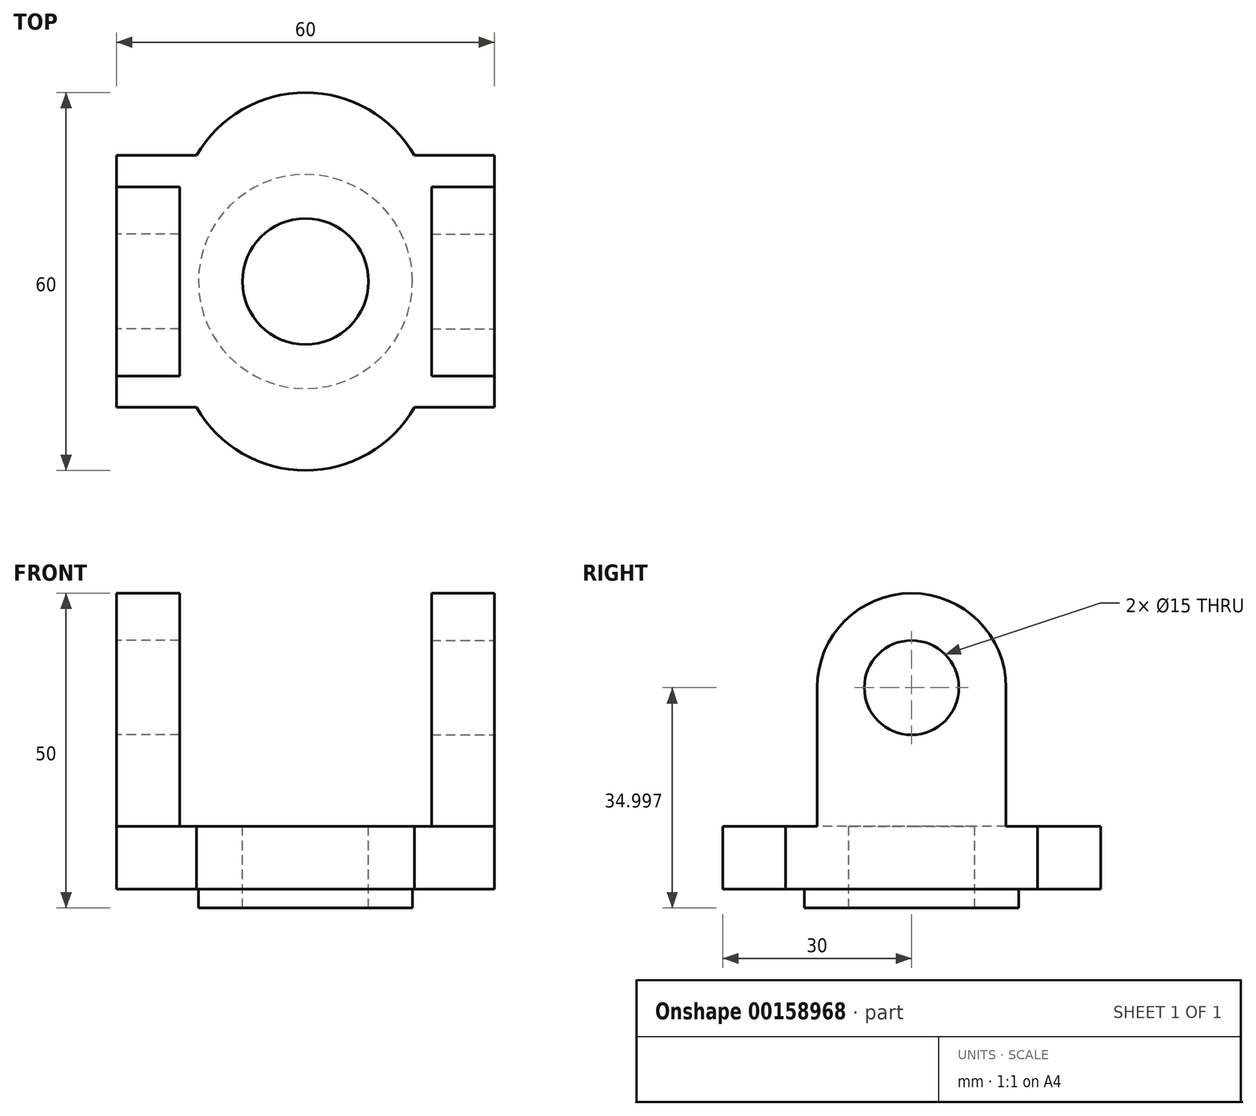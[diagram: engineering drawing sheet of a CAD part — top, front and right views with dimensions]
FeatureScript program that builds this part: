
annotation { "Feature Type Name" : "Feature", "Feature Type Description" : "" }
export const myFeature = defineFeature(function(context is Context, id is Id, definition is map)
    precondition{}
    {
        {
            var Q0;
            Q0=qCreatedBy(makeId("Front.planeOp"),FACE);
            var sketch = newSketch(context, id + "F0", { "sketchPlane" : qUnion([Q0])});
            skLineSegment(sketch, "E0.bottom", {"start": v(-30, -5.63) * mm, "end": v(30, -5.63) * mm});
            skLineSegment(sketch, "E0.top", {"start": v(-30, 4.37) * mm, "end": v(30, 4.37) * mm});
            skLineSegment(sketch, "E0.left", {"start": v(-30, -5.63) * mm, "end": v(-30, 4.37) * mm});
            skLineSegment(sketch, "E0.right", {"start": v(30, -5.63) * mm, "end": v(30, 4.37) * mm});
            skPoint(sketch, "E1", {"position": v(0, 4.37) * mm});
            skPoint(sketch, "E1.positionSnap0", {"position": v(0, 4.37) * mm});
            skSolve(sketch);
        }
        {
            var Q0;
            Q0 = qSketchRegion(id + "F0", true);
            extrude(context, id + "F1", {"entities" : qUnion([Q0]), "oppositeDirection" : true, "depth" : 40 * mm});
        }
        {
            var Q0;
            Q0=makeQuery(id+"F1.opExtrude","SWEPT_FACE",FACE,{"disambiguationData":[OSD([sQuery(id+"F0.wireOp",EDGE,"E0.right")])]});
            var sketch = newSketch(context, id + "F2", { "sketchPlane" : qUnion([Q0])});
            skPoint(sketch, "E2", {"position": v(20, 4.37) * mm});
            skCircle(sketch, "E3", {"center": v(20, 26.37) * mm, "radius": 7.5 * mm});
            skLineSegment(sketch, "E4", {"start": v(5, 4.37) * mm, "end": v(5, 26.37) * mm});
            skPoint(sketch, "E5", {"position": v(35, 4.37) * mm});
            skLineSegment(sketch, "E6", {"start": v(35, 4.37) * mm, "end": v(35, 26.37) * mm});
            skArc(sketch, "E7", {"start": v(35, 26.37) * mm, "mid": v(20, 41.37) * mm, "end": v(5, 26.37) * mm});
            skLineSegment(sketch, "E8", {"start": v(5, 4.37) * mm, "end": v(35, 4.37) * mm});
            skSolve(sketch);
        }
        {
            var Q0;
            Q0 = qSketchRegion(id + "F2", true);
            extrude(context, id + "F3", {"entities" : qUnion([Q0]), "operationType" : NewBodyOperationType.ADD, "oppositeDirection" : true, "depth" : 10 * mm});
        }
        {
            var Q0;
            Q0=makeQuery(id+"F1.opExtrude","SWEPT_FACE",FACE,{"disambiguationData":[OSD([sQuery(id+"F0.wireOp",EDGE,"E0.left")])]});
            var sketch = newSketch(context, id + "F4", { "sketchPlane" : qUnion([Q0])});
            skPoint(sketch, "E9", {"position": v(-35, 4.37) * mm});
            skPoint(sketch, "E10", {"position": v(-5, 4.37) * mm});
            skLineSegment(sketch, "E11.0.0", {"start": v(-5, 4.37) * mm, "end": v(-5, 26.37) * mm});
            skArc(sketch, "E11.0.1", {"start": v(-5, 26.37) * mm, "mid": v(-20, 41.37) * mm, "end": v(-35, 26.37) * mm});
            skLineSegment(sketch, "E11.0.2", {"start": v(-35, 26.37) * mm, "end": v(-35, 4.37) * mm});
            skLineSegment(sketch, "E11.0.3", {"start": v(-35, 4.37) * mm, "end": v(-5, 4.37) * mm});
            skCircle(sketch, "E12.0.0", {"center": v(-20, 26.37) * mm, "radius": 7.5 * mm});
            skSolve(sketch);
        }
        {
            var Q0;
            Q0 = qSketchRegion(id + "F4", true);
            extrude(context, id + "F5", {"entities" : qUnion([Q0]), "operationType" : NewBodyOperationType.ADD, "oppositeDirection" : true, "depth" : 10 * mm});
        }
        {
            var Q0;
            Q0=makeQuery(id+"F1.opExtrude","SWEPT_FACE",FACE,{"disambiguationData":[OSD([sQuery(id+"F0.wireOp",EDGE,"E0.bottom")])]});
            var sketch = newSketch(context, id + "F6", { "sketchPlane" : qUnion([Q0])});
            skCircle(sketch, "E13", {"center": v(0, -20) * mm, "radius": 17 * mm});
            skPoint(sketch, "E14", {"position": v(0, -40) * mm});
            skLineSegment(sketch, "E15", {"start": v(0, -40) * mm, "end": v(0, -20) * mm, "construction": true});
            skSolve(sketch);
        }
        {
            var Q0;
            Q0 = qSketchRegion(id + "F6", true);
            extrude(context, id + "F7", {"entities" : qUnion([Q0]), "operationType" : NewBodyOperationType.ADD, "depth" : 3 * mm});
        }
        {
            var Q0;
            Q0=makeQuery(id+"F1.opExtrude","SWEPT_FACE",FACE,{"disambiguationData":[OSD([sQuery(id+"F0.wireOp",EDGE,"E0.top")])]});
            var sketch = newSketch(context, id + "F8", { "sketchPlane" : qUnion([Q0])});
            skLineSegment(sketch, "E16", {"start": v(-30, 20) * mm, "end": v(30, 20) * mm, "construction": true});
            skLineSegment(sketch, "E17", {"start": v(0, 0) * mm, "end": v(0, 40) * mm, "construction": true});
            skCircle(sketch, "E18", {"center": v(0, 20) * mm, "radius": 10 * mm});
            skLineSegment(sketch, "E19", {"start": v(0, 20) * mm, "end": v(10, 20) * mm, "construction": true});
            skSolve(sketch);
        }
        {
            var Q0;
            Q0 = qSketchRegion(id + "F8", true);
            extrude(context, id + "F9", {"entities" : qUnion([Q0]), "operationType" : NewBodyOperationType.REMOVE, "oppositeDirection" : true, "depth" : 25 * mm});
        }
        {
            var Q0;
            Q0=makeQuery(id+"F1.opExtrude","SWEPT_FACE",FACE,{"disambiguationData":[OSD([sQuery(id+"F0.wireOp",EDGE,"E0.top")])]});
            var sketch = newSketch(context, id + "F10", { "sketchPlane" : qUnion([Q0])});
            skArc(sketch, "E20", {"start": v(-17.32, 0) * mm, "mid": v(0, -10) * mm, "end": v(17.32, 0) * mm});
            skArc(sketch, "E21", {"start": v(17.32, 40) * mm, "mid": v(0, 50) * mm, "end": v(-17.32, 40) * mm});
            skLineSegment(sketch, "E22", {"start": v(-17.32, 0) * mm, "end": v(17.32, 0) * mm});
            skLineSegment(sketch, "E23", {"start": v(-17.32, 40) * mm, "end": v(17.32, 40) * mm});
            skSolve(sketch);
        }
        {
            var Q0;
            Q0 = qSketchRegion(id + "F10", true);
            extrude(context, id + "F11", {"entities" : qUnion([Q0]), "operationType" : NewBodyOperationType.ADD, "oppositeDirection" : true, "depth" : 10 * mm});
        }
    });
